# Revit family: BK-BK Inverted Roof 90mm Family
name_source: partatom
category: Generic Models
revit_build: Autodesk Revit 2017 (Build: 20160225_1515(x64)
units: mm (PartAtom-declared; Revit-internal decimal feet)

## family parameters
Always vertical = Yes
Can host rebar = No
Cut with Voids When Loaded = No
Host = Floor
Part Type = Normal
Room Calculation Point = No
Round Connector Dimension = Use Diameter
Shared = No

## types (1)
- Lambdaboard
    Density = 40.0000 kg/m³
    Depth = 90 mm  [stored 0.295276 ft]
    Description = Flexible PIR Insulation
    Length = 4000 mm
    Manufacturer = Lambdaboard
    Material = Polyisocyanurate
    Model = BK/BK Inverted Roof 90mm
    Slab Thickness = 300 mm  [stored 0.984252 ft]
    Thermal Conductivity = 0.0240 W/(m·K)
    Thermal Resistance = 3.7500 (m²·K)/W
    URL = www.rigifoam.com
    Width = 4000 mm

note: [stored X ft] marks values corroborated as IEEE doubles in the binary element streams (Revit-internal decimal feet)

## geometry (parser evidence)
native form markers: Sweep x2
no freeform markers — native parametric forms only
